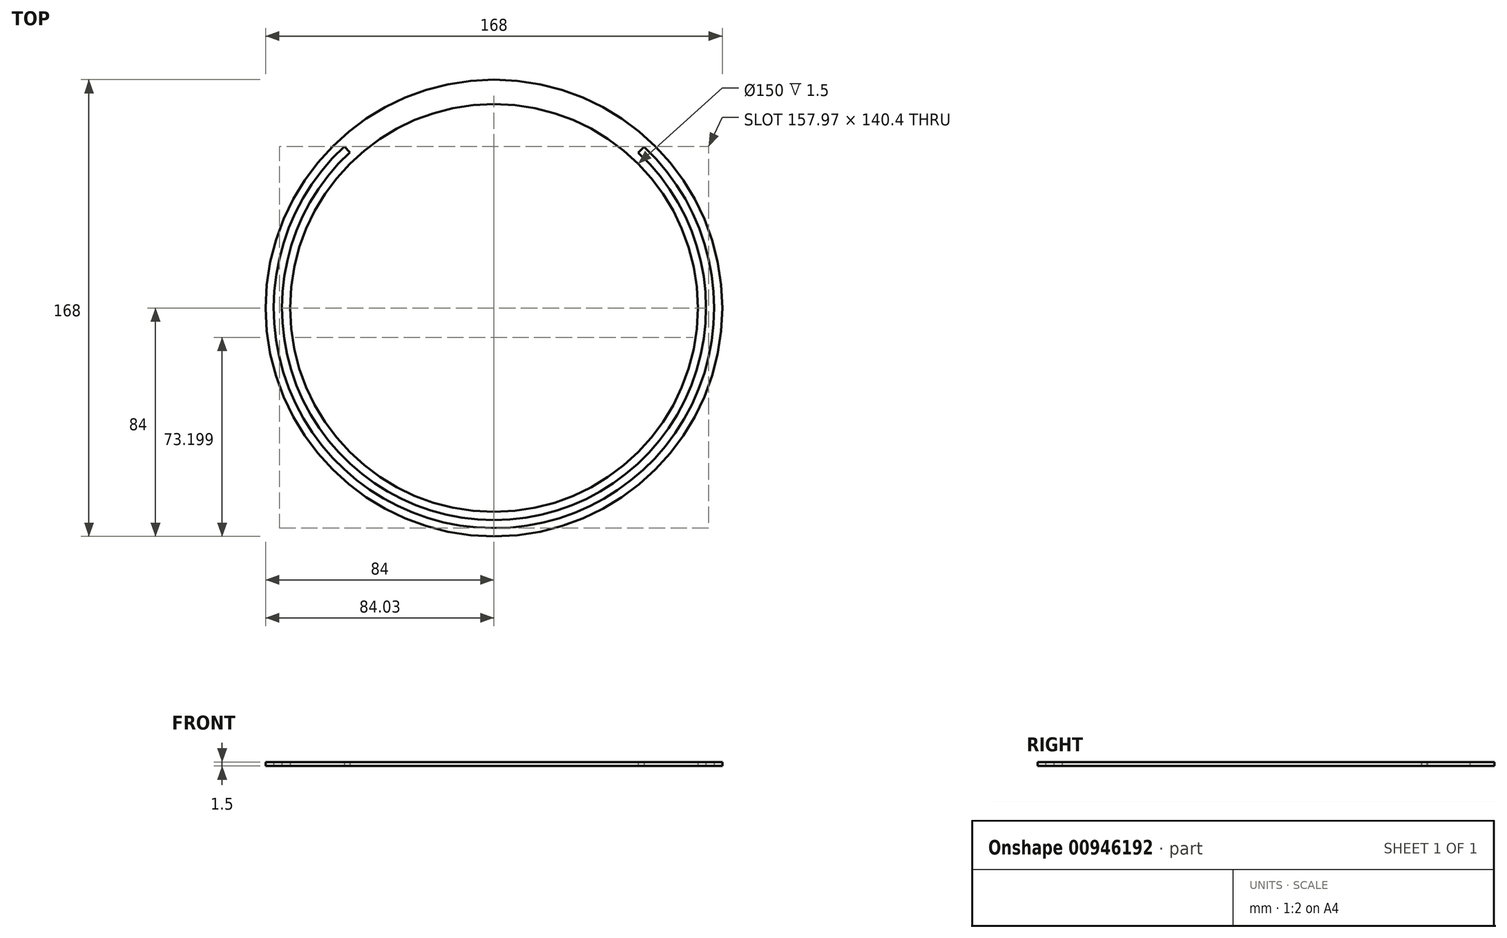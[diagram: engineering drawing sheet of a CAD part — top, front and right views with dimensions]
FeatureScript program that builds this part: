
annotation { "Feature Type Name" : "Feature", "Feature Type Description" : "" }
export const myFeature = defineFeature(function(context is Context, id is Id, definition is map)
    precondition{}
    {
        {
            var Q0;
            Q0=qCreatedBy(makeId("Top.planeOp"),FACE);
            var sketch = newSketch(context, id + "F0", { "sketchPlane" : qUnion([Q0])});
            skCircle(sketch, "E0", {"center": v(0, 0) * mm, "radius": 84 * mm});
            skCircle(sketch, "E1", {"center": v(0, 0) * mm, "radius": 81 * mm});
            skCircle(sketch, "E2", {"center": v(0, 0) * mm, "radius": 78 * mm});
            skCircle(sketch, "E3", {"center": v(0, 0) * mm, "radius": 75 * mm});
            skLineSegment(sketch, "E4", {"start": v(-53.03, 57.2) * mm, "end": v(-55.07, 59.4) * mm});
            skLineSegment(sketch, "E5", {"start": v(53.09, 57.14) * mm, "end": v(55.27, 59.21) * mm});
            skSolve(sketch);
        }
        {
            var Q0;
            Q0=makeQuery(id+"F0.imprint","IMPRINT",FACE,{"disambiguationData":[TD([[makeQuery(id+"F0.imprint","IMPRINT",EDGE,{"derivedFrom":sQuery(id+"F0.wireOp",EDGE,"E0")}),1.0]])]});
            var Q1;
            {var subQ0=sQuery(id+"F0.wireOp",EDGE,"E4");Q1=makeQuery(id+"F0.imprint","IMPRINT",FACE,{"disambiguationData":[TD([[makeQuery(id+"F0.imprint","IMPRINT",EDGE,{"derivedFrom":subQ0}),-1.0]])]});}
            var Q2;
            Q2=makeQuery(id+"F0.imprint","IMPRINT",FACE,{"disambiguationData":[TD([[makeQuery(id+"F0.imprint","IMPRINT",EDGE,{"derivedFrom":sQuery(id+"F0.wireOp",EDGE,"E3")}),-1.0]])]});
            extrude(context, id + "F1", {"entities" : qUnion([Q0, Q1, Q2]), "depth" : 1.5 * mm, "offsetDistance" : 25 * mm});
        }
    });
